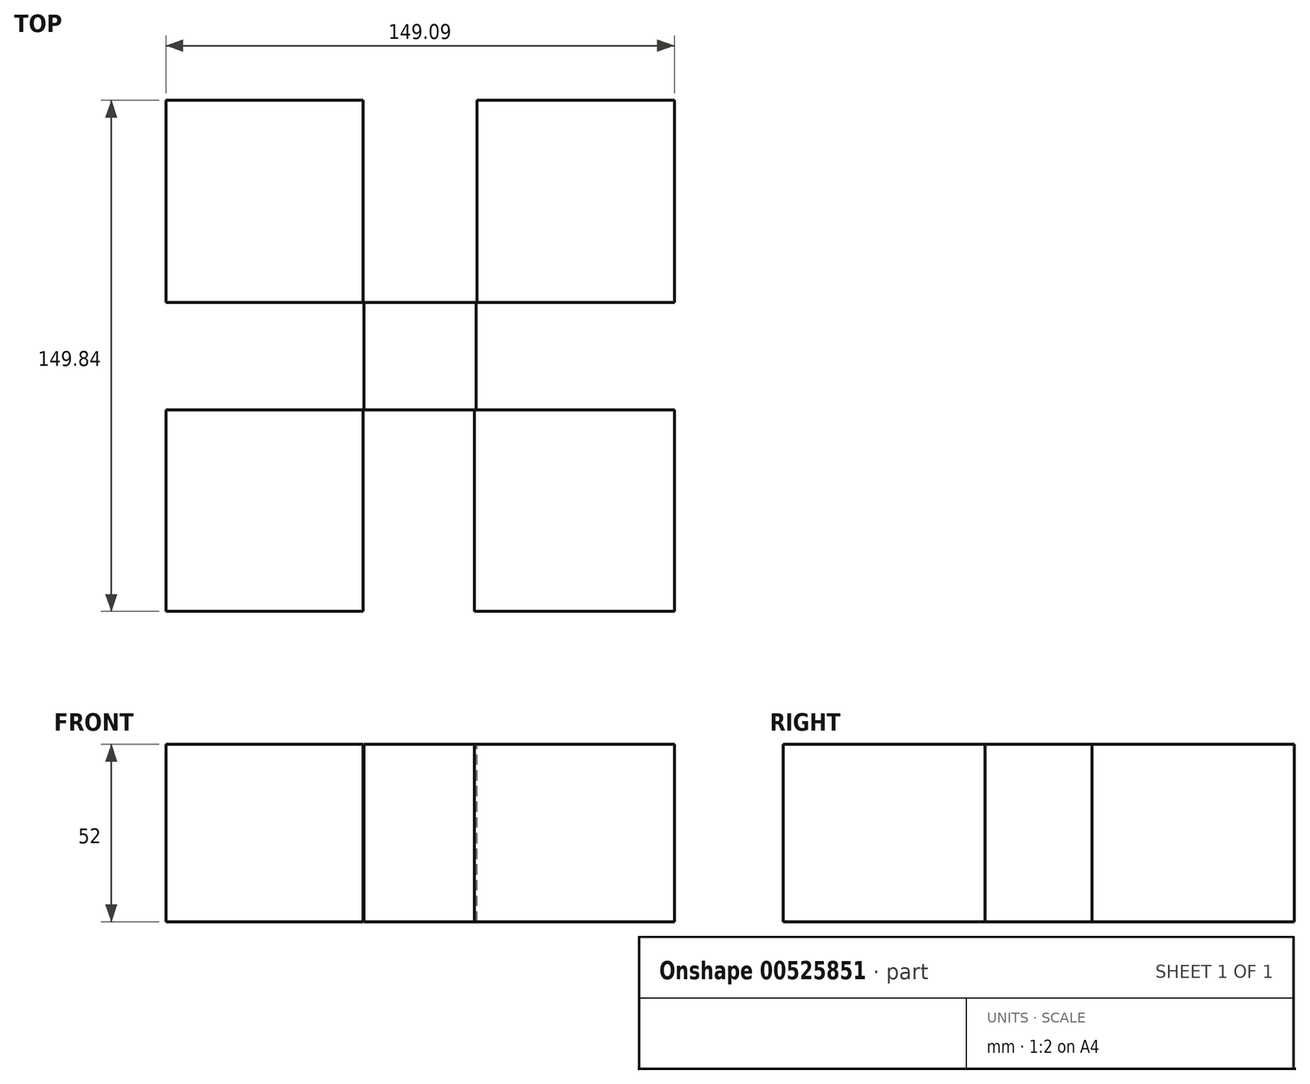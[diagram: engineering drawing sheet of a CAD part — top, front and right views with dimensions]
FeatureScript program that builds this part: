
annotation { "Feature Type Name" : "Feature", "Feature Type Description" : "" }
export const myFeature = defineFeature(function(context is Context, id is Id, definition is map)
    precondition{}
    {
        {
            var Q0;
            Q0=qCreatedBy(makeId("Top.planeOp"),FACE);
            var sketch = newSketch(context, id + "F0", { "sketchPlane" : qUnion([Q0])});
            skLineSegment(sketch, "E0.bottom", {"start": v(0, 0) * mm, "end": v(16.54, 0) * mm});
            skLineSegment(sketch, "E0.top", {"start": v(0, 16) * mm, "end": v(16.54, 16) * mm});
            skLineSegment(sketch, "E0.left", {"start": v(0, 0) * mm, "end": v(0, 16) * mm});
            skLineSegment(sketch, "E0.right", {"start": v(16.54, 0) * mm, "end": v(16.54, 16) * mm});
            skLineSegment(sketch, "E1.bottom", {"start": v(0, 0) * mm, "end": v(-16.33, 0) * mm});
            skLineSegment(sketch, "E1.top", {"start": v(0, 16) * mm, "end": v(-16.33, 16) * mm});
            skLineSegment(sketch, "E1.right", {"start": v(-16.33, 0) * mm, "end": v(-16.33, 16) * mm});
            skLineSegment(sketch, "E2.top", {"start": v(0, -15.48) * mm, "end": v(-16.33, -15.48) * mm});
            skLineSegment(sketch, "E2.left", {"start": v(0, 0) * mm, "end": v(0, -15.48) * mm});
            skLineSegment(sketch, "E2.right", {"start": v(-16.33, 0) * mm, "end": v(-16.33, -15.48) * mm});
            skLineSegment(sketch, "E3.top", {"start": v(0, -15.48) * mm, "end": v(16.54, -15.48) * mm});
            skLineSegment(sketch, "E3.right", {"start": v(16.54, 0) * mm, "end": v(16.54, -15.48) * mm});
            skSolve(sketch);
        }
        {
            var Q0;
            Q0=qCreatedBy(makeId("Top.planeOp"),FACE);
            var sketch = newSketch(context, id + "F1", { "sketchPlane" : qUnion([Q0])});
            skLineSegment(sketch, "E4.bottom", {"start": v(-74.42, 75.29) * mm, "end": v(-16.57, 75.29) * mm});
            skLineSegment(sketch, "E4.top", {"start": v(-74.42, 15.95) * mm, "end": v(-16.57, 15.95) * mm});
            skLineSegment(sketch, "E4.left", {"start": v(-74.42, 75.29) * mm, "end": v(-74.42, 15.95) * mm});
            skLineSegment(sketch, "E4.right", {"start": v(-16.57, 75.29) * mm, "end": v(-16.57, 15.95) * mm});
            skLineSegment(sketch, "E5.bottom", {"start": v(74.67, 75.29) * mm, "end": v(16.81, 75.29) * mm});
            skLineSegment(sketch, "E5.top", {"start": v(74.67, 15.95) * mm, "end": v(16.81, 15.95) * mm});
            skLineSegment(sketch, "E5.left", {"start": v(74.67, 75.29) * mm, "end": v(74.67, 15.95) * mm});
            skLineSegment(sketch, "E5.right", {"start": v(16.81, 75.29) * mm, "end": v(16.81, 15.95) * mm});
            skLineSegment(sketch, "E6.bottom", {"start": v(-16.57, -15.45) * mm, "end": v(-74.42, -15.45) * mm});
            skLineSegment(sketch, "E6.top", {"start": v(-16.57, -74.55) * mm, "end": v(-74.42, -74.55) * mm});
            skLineSegment(sketch, "E6.left", {"start": v(-16.57, -15.45) * mm, "end": v(-16.57, -74.55) * mm});
            skLineSegment(sketch, "E6.right", {"start": v(-74.42, -15.45) * mm, "end": v(-74.42, -74.55) * mm});
            skLineSegment(sketch, "E7.bottom", {"start": v(16.07, -15.45) * mm, "end": v(74.67, -15.45) * mm});
            skLineSegment(sketch, "E7.top", {"start": v(16.07, -74.55) * mm, "end": v(74.67, -74.55) * mm});
            skLineSegment(sketch, "E7.left", {"start": v(16.07, -15.45) * mm, "end": v(16.07, -74.55) * mm});
            skLineSegment(sketch, "E7.right", {"start": v(74.67, -15.45) * mm, "end": v(74.67, -74.55) * mm});
            skSolve(sketch);
        }
        {
            var Q0;
            Q0=makeQuery(id+"F1.imprint","IMPRINT",FACE,{"disambiguationData":[TD([[makeQuery(id+"F1.imprint","IMPRINT",EDGE,{"derivedFrom":sQuery(id+"F1.wireOp",EDGE,"E6.bottom")}),1.0]])]});
            var Q1;
            Q1=makeQuery(id+"F1.imprint","IMPRINT",FACE,{"disambiguationData":[TD([[makeQuery(id+"F1.imprint","IMPRINT",EDGE,{"derivedFrom":sQuery(id+"F1.wireOp",EDGE,"E7.bottom")}),-1.0]])]});
            var Q2;
            Q2=makeQuery(id+"F1.imprint","IMPRINT",FACE,{"disambiguationData":[TD([[makeQuery(id+"F1.imprint","IMPRINT",EDGE,{"derivedFrom":sQuery(id+"F1.wireOp",EDGE,"E5.bottom")}),1.0]])]});
            var Q3;
            Q3=makeQuery(id+"F0.imprint","IMPRINT",FACE,{"disambiguationData":[TD([[makeQuery(id+"F0.imprint","IMPRINT",EDGE,{"derivedFrom":sQuery(id+"F0.wireOp",EDGE,"E0.top")}),-1.0]])]});
            var Q4;
            Q4=makeQuery(id+"F1.imprint","IMPRINT",FACE,{"disambiguationData":[TD([[makeQuery(id+"F1.imprint","IMPRINT",EDGE,{"derivedFrom":sQuery(id+"F1.wireOp",EDGE,"E4.bottom")}),-1.0]])]});
            var Q5;
            Q5=makeQuery(id+"F0.imprint","IMPRINT",FACE,{"disambiguationData":[TD([[makeQuery(id+"F0.imprint","IMPRINT",EDGE,{"derivedFrom":sQuery(id+"F0.wireOp",EDGE,"E1.bottom")}),1.0]])]});
            var Q6;
            Q6=makeQuery(id+"F0.imprint","IMPRINT",FACE,{"disambiguationData":[TD([[makeQuery(id+"F0.imprint","IMPRINT",EDGE,{"derivedFrom":sQuery(id+"F0.wireOp",EDGE,"E1.top")}),1.0]])]});
            var Q7;
            Q7=makeQuery(id+"F0.imprint","IMPRINT",FACE,{"disambiguationData":[TD([[makeQuery(id+"F0.imprint","IMPRINT",EDGE,{"derivedFrom":sQuery(id+"F0.wireOp",EDGE,"E0.bottom")}),-1.0]])]});
            extrude(context, id + "F2", {"entities" : qUnion([Q0, Q1, Q2, Q3, Q4, Q5, Q6, Q7]), "oppositeDirection" : true, "depth" : 52 * mm, "offsetDistance" : 25 * mm});
        }
    });
